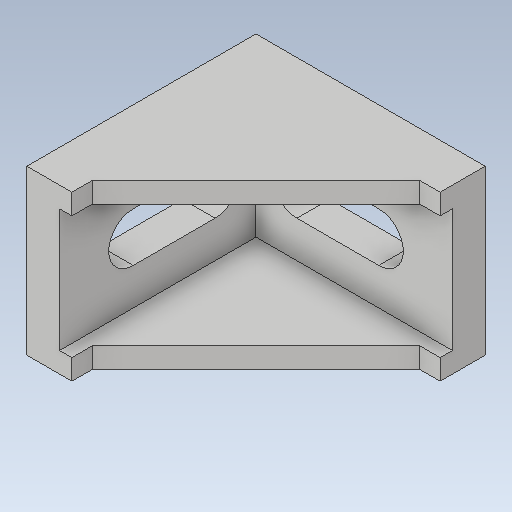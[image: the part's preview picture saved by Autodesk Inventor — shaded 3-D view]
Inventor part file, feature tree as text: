
AUTODESK INVENTOR PART (.ipt)
format: ipt  version: 2020 (Build 240168000, 168)  size: 215,040 bytes
history: native  units: mm
features: extrude x8, sketch x8, projected_geometry x8
ambient origin geometry x8: Origin, YZ Plane, XZ Plane, XY Plane, X Axis, Y Axis, Z Axis, Center Point
bodies: Solid1 (feature_tree)
feature tree (24):
  extrude  "Extrusion1"  Depth=28.0mm
  extrude  "Extrusion2"  Depth=10.0mm
  extrude  "Extrusion3"  Depth=6.0mm
  extrude  "Extrusion4"  Depth=4.0mm
  extrude  "Extrusion5"  Depth=10.0mm
  extrude  "Extrusion6"  Depth=6.0mm
  extrude  "Extrusion7"  Depth=1.0mm
  extrude  "Extrusion8"  Depth=1.0mm
  sketch  "Sketch1"  dims[d0=20.0mm d1=28.0mm]
  sketch  "Sketch2"  dims[d2=4.0mm d3=0.0mm d4=10.0mm]
  projected_geometry  "Projected Loop1"
  sketch  "Sketch3"  dims[d5=6.0mm d6=9.0mm]
  projected_geometry  "Projected Loop2"
  sketch  "Sketch4"  dims[d7=30.0mm d8=0.0mm d9=4.0mm]
  projected_geometry  "Projected Loop3"
  sketch  "Sketch5"  dims[d10=24.0mm d11=0.0mm d12=10.0mm]
  projected_geometry  "Projected Loop4"
  sketch  "Sketch6"  dims[d13=6.0mm d14=9.0mm]
  projected_geometry  "Projected Loop5"
  sketch  "Sketch7"  dims[d15=24.0mm d16=0.0mm d17=1.0mm]
  projected_geometry  "Projected Loop6"
  sketch  "Sketch8"  dims[d18=5.8mm d19=1.0mm d20=1.0mm d21=0.0mm d22=1.0mm d23=5.8mm d24=1.0mm d25=1.0mm d26=0.0mm d27=1.5mm d28=2.5mm d29=1.5mm d30=2.5mm d31=2.5mm d32=0.0mm d33=2.5mm d34=0.0mm]
  projected_geometry  "Projected Loop7"
  projected_geometry  "Projected Loop8"
